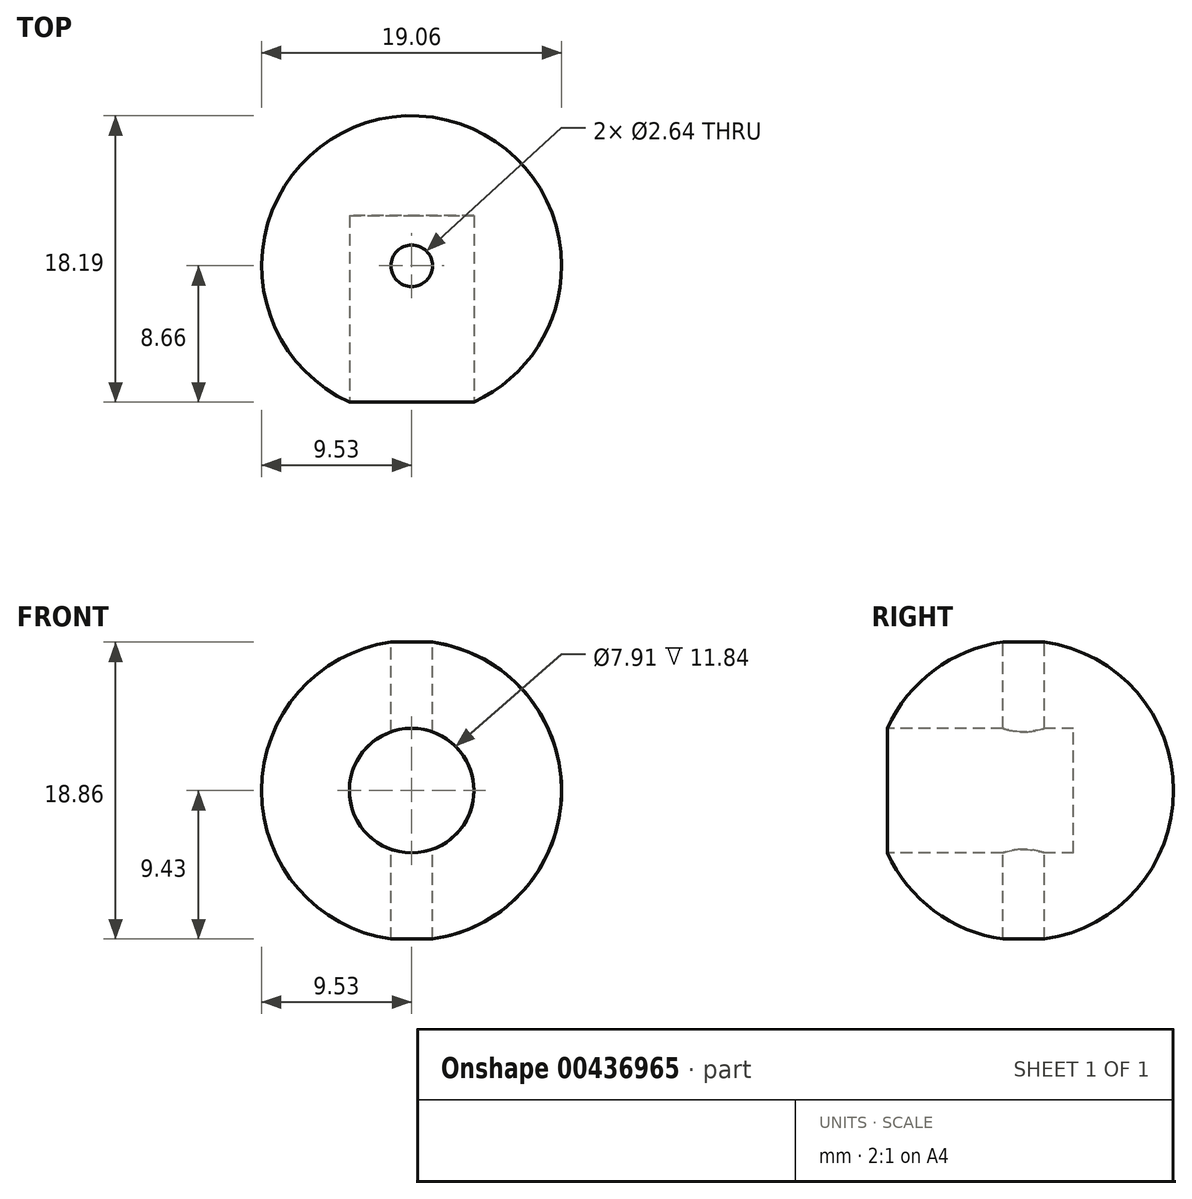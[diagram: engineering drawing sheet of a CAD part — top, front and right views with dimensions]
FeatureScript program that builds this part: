
annotation { "Feature Type Name" : "Feature", "Feature Type Description" : "" }
export const myFeature = defineFeature(function(context is Context, id is Id, definition is map)
    precondition{}
    {
        {
            var Q0;
            Q0=qCreatedBy(makeId("Front.planeOp"),FACE);
            var sketch = newSketch(context, id + "F0", { "sketchPlane" : qUnion([Q0])});
            skArc(sketch, "E0", {"start": v(0, -9.53) * mm, "mid": v(9.53, 0) * mm, "end": v(0, 9.53) * mm});
            skLineSegment(sketch, "E1", {"start": v(0, 9.53) * mm, "end": v(0, -9.53) * mm});
            skLineSegment(sketch, "E2", {"start": v(0, 0) * mm, "end": v(28.29, 0) * mm, "construction": true});
            skPoint(sketch, "E2.endSnap0", {"position": v(9.53, 0) * mm});
            skLineSegment(sketch, "E3", {"start": v(28.29, 0) * mm, "end": v(0, 0) * mm, "construction": true});
            skLineSegment(sketch, "E4", {"start": v(0, 0) * mm, "end": v(-27.51, 0) * mm, "construction": true});
            skSolve(sketch);
        }
        {
            var Q0;
            Q0=makeQuery(id+"F0.imprint","IMPRINT",FACE,{"disambiguationData":[TD([[makeQuery(id+"F0.imprint","IMPRINT",EDGE,{"derivedFrom":sQuery(id+"F0.wireOp",EDGE,"E0")}),1.0]])]});
            var Q1;
            Q1=sQuery(id+"F0.wireOp",EDGE,"E1");
            revolve(context, id + "F1", {"entities" : qUnion([Q0]), "axis" : qUnion([Q1]), "revolveType" : RevolveType.FULL});
        }
        {
            var Q0;
            Q0=qCreatedBy(makeId("Front.planeOp"),FACE);
            cPlane(context, id + "F2", {"entities" : qUnion([Q0]), "cplaneType" : CPlaneType.OFFSET, "offset" : 9.52 * mm, "width" : 152.4 * mm, "height" : 152.4 * mm});
        }
        {
            var Q0;
            Q0=qCreatedBy(id+"F2.planeOp",FACE);
            var sketch = newSketch(context, id + "F3", { "sketchPlane" : qUnion([Q0])});
            skCircle(sketch, "E5", {"center": v(0, 0) * mm, "radius": 3.96 * mm});
            skSolve(sketch);
        }
        {
            var Q0;
            Q0=qSketchRegion(id+"F3",true);
            extrude(context, id + "F4", {"entities" : qUnion([Q0]), "operationType" : NewBodyOperationType.REMOVE, "oppositeDirection" : true, "depth" : 12.7 * mm});
        }
        {
            var Q0;
            Q0=qCreatedBy(makeId("Top.planeOp"),FACE);
            cPlane(context, id + "F5", {"entities" : qUnion([Q0]), "cplaneType" : CPlaneType.OFFSET, "offset" : 9.52 * mm, "width" : 152.4 * mm, "height" : 152.4 * mm});
        }
        {
            var Q0;
            Q0=qCreatedBy(id+"F5.planeOp",FACE);
            var sketch = newSketch(context, id + "F6", { "sketchPlane" : qUnion([Q0])});
            skCircle(sketch, "E6", {"center": v(0, 0) * mm, "radius": 1.32 * mm});
            skSolve(sketch);
        }
        {
            var Q0;
            Q0=qSketchRegion(id+"F6",true);
            extrude(context, id + "F7", {"entities" : qUnion([Q0]), "operationType" : NewBodyOperationType.REMOVE, "endBound" : BoundingType.THROUGH_ALL, "oppositeDirection" : true, "depth" : 25.4 * mm});
        }
    });
